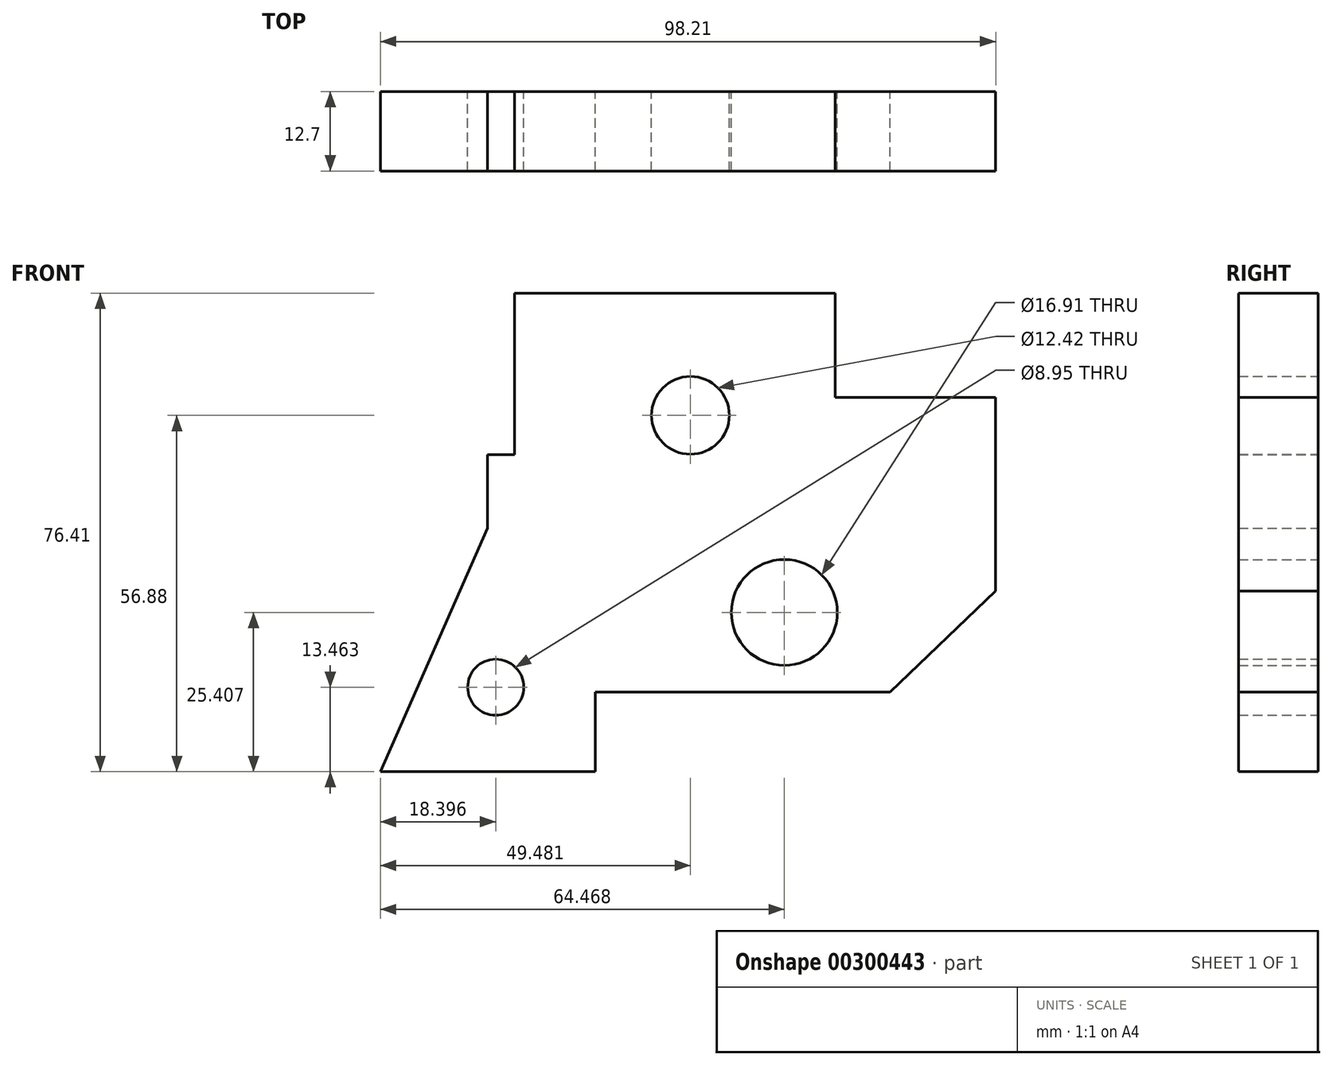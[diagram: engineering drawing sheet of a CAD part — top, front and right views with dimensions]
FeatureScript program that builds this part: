
annotation { "Feature Type Name" : "Feature", "Feature Type Description" : "" }
export const myFeature = defineFeature(function(context is Context, id is Id, definition is map)
    precondition{}
    {
        {
            var Q0;
            Q0=qCreatedBy(makeId("Front.planeOp"),FACE);
            var sketch = newSketch(context, id + "F0", { "sketchPlane" : qUnion([Q0])});
            skLineSegment(sketch, "E0", {"start": v(-9.67, 47.59) * mm, "end": v(41.52, 47.59) * mm});
            skLineSegment(sketch, "E1", {"start": v(41.52, 47.59) * mm, "end": v(41.52, 30.9) * mm});
            skLineSegment(sketch, "E2", {"start": v(41.52, 30.9) * mm, "end": v(67.12, 30.9) * mm});
            skLineSegment(sketch, "E3", {"start": v(67.12, 30.9) * mm, "end": v(67.12, 0) * mm});
            skLineSegment(sketch, "E4", {"start": v(67.12, 0) * mm, "end": v(50.24, -16.12) * mm});
            skLineSegment(sketch, "E5", {"start": v(50.24, -16.12) * mm, "end": v(3.22, -16.12) * mm});
            skLineSegment(sketch, "E6", {"start": v(3.22, -16.12) * mm, "end": v(3.22, -28.82) * mm});
            skLineSegment(sketch, "E7", {"start": v(3.22, -28.82) * mm, "end": v(-31.1, -28.82) * mm});
            skLineSegment(sketch, "E8", {"start": v(-31.1, -28.82) * mm, "end": v(-14.03, 10.05) * mm});
            skLineSegment(sketch, "E9", {"start": v(-14.03, 10.05) * mm, "end": v(-14.03, 21.8) * mm});
            skLineSegment(sketch, "E10", {"start": v(-14.03, 21.8) * mm, "end": v(-9.67, 21.8) * mm});
            skLineSegment(sketch, "E11", {"start": v(-9.67, 21.8) * mm, "end": v(-9.67, 47.59) * mm});
            skCircle(sketch, "E12", {"center": v(18.4, 28.06) * mm, "radius": 6.21 * mm});
            skCircle(sketch, "E13", {"center": v(33.38, -3.41) * mm, "radius": 8.46 * mm});
            skCircle(sketch, "E14", {"center": v(-12.7, -15.36) * mm, "radius": 4.47 * mm});
            skSolve(sketch);
        }
        {
            var Q0;
            Q0 = qSketchRegion(id + "F0", true);
            var Q1;
            Q1=makeQuery(id+"F0.imprint","IMPRINT",FACE,{"disambiguationData":[TD([[makeQuery(id+"F0.imprint","IMPRINT",EDGE,{"derivedFrom":sQuery(id+"F0.wireOp",EDGE,"E0")}),-1.0]])]});
            extrude(context, id + "F1", {"entities" : qUnion([Q0, Q1]), "depth" : 12.7 * mm});
        }
        {
            var Q0;
            Q0 = qSketchRegion(id + "F0", true);
            extrude(context, id + "F2", {"entities" : qUnion([Q0]), "operationType" : NewBodyOperationType.ADD, "depth" : 12.7 * mm});
        }
    });
